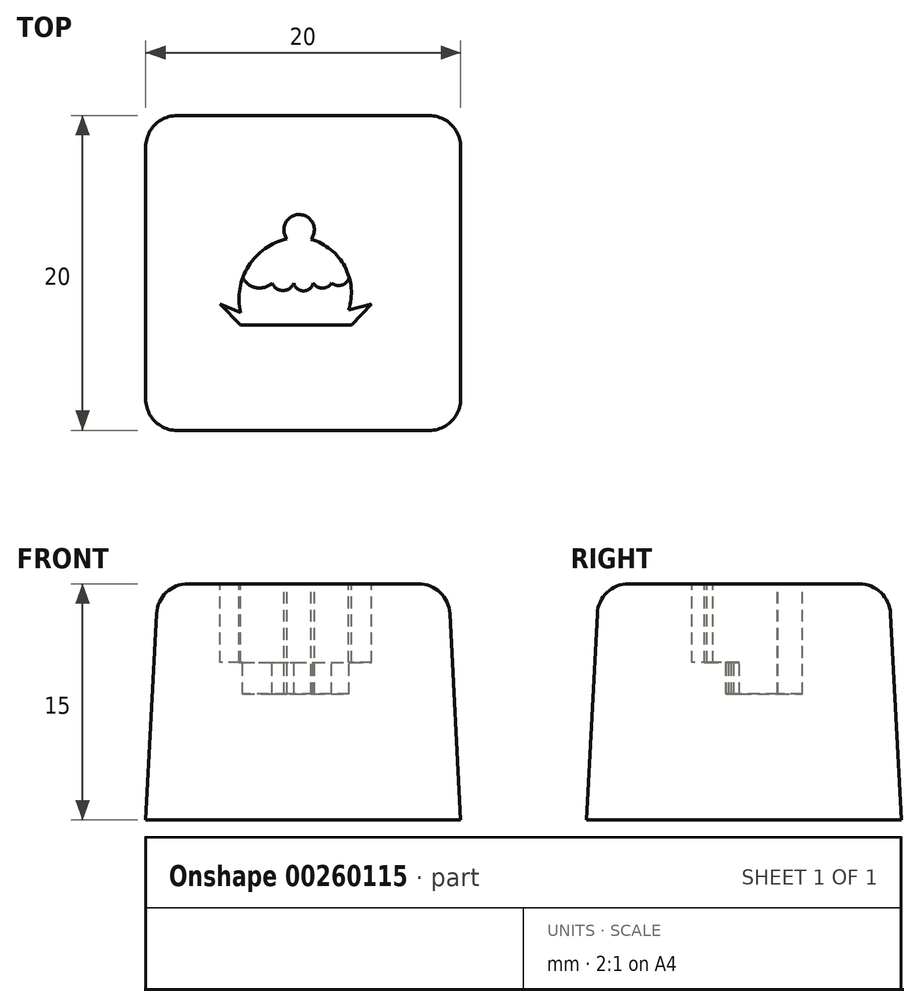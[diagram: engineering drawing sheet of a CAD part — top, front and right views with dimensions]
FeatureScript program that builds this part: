
annotation { "Feature Type Name" : "Feature", "Feature Type Description" : "" }
export const myFeature = defineFeature(function(context is Context, id is Id, definition is map)
    precondition{}
    {
        {
            var Q0;
            Q0=qCreatedBy(makeId("Top.planeOp"),FACE);
            var sketch = newSketch(context, id + "F0", { "sketchPlane" : qUnion([Q0])});
            skLineSegment(sketch, "E0.bottom", {"start": v(-8.03, 10.29) * mm, "end": v(11.97, 10.29) * mm});
            skLineSegment(sketch, "E0.top", {"start": v(-8.03, -9.71) * mm, "end": v(11.97, -9.71) * mm});
            skLineSegment(sketch, "E0.left", {"start": v(-8.03, 10.29) * mm, "end": v(-8.03, -9.71) * mm});
            skLineSegment(sketch, "E0.right", {"start": v(11.97, 10.29) * mm, "end": v(11.97, -9.71) * mm});
            skSolve(sketch);
        }
        {
            var Q0;
            Q0 = qSketchRegion(id + "F0", true);
            extrude(context, id + "F1", {"entities" : qUnion([Q0]), "depth" : 15 * mm, "hasDraft" : true, "draftAngle" : 3 * degree, "draftPullDirection" : true});
        }
        {
            var Q0;
            Q0=makeQuery(id+"F1.opExtrude","SWEPT_EDGE",EDGE,{"disambiguationData":[OSD([sQuery(id+"F0.wireOp",EDGE,"E0.bottom"),sQuery(id+"F0.wireOp",EDGE,"E0.right")])]});
            var Q1;
            Q1=makeQuery(id+"F1.opExtrude","CAP_EDGE",EDGE,{"disambiguationData":[OSD([sQuery(id+"F0.wireOp",EDGE,"E0.bottom")])],"isStart":false});
            var Q2;
            Q2=makeQuery(id+"F1.opExtrude","SWEPT_EDGE",EDGE,{"disambiguationData":[OSD([sQuery(id+"F0.wireOp",EDGE,"E0.bottom"),sQuery(id+"F0.wireOp",EDGE,"E0.left")])]});
            var Q3;
            Q3=makeQuery(id+"F1.opExtrude","CAP_EDGE",EDGE,{"disambiguationData":[OSD([sQuery(id+"F0.wireOp",EDGE,"E0.right")])],"isStart":false});
            var Q4;
            Q4=makeQuery(id+"F1.opExtrude","SWEPT_EDGE",EDGE,{"disambiguationData":[OSD([sQuery(id+"F0.wireOp",EDGE,"E0.top"),sQuery(id+"F0.wireOp",EDGE,"E0.right")])]});
            var Q5;
            Q5=makeQuery(id+"F1.opExtrude","CAP_EDGE",EDGE,{"disambiguationData":[OSD([sQuery(id+"F0.wireOp",EDGE,"E0.top")])],"isStart":false});
            var Q6;
            Q6=makeQuery(id+"F1.opExtrude","CAP_EDGE",EDGE,{"disambiguationData":[OSD([sQuery(id+"F0.wireOp",EDGE,"E0.left")])],"isStart":false});
            var Q7;
            Q7=makeQuery(id+"F1.opExtrude","SWEPT_EDGE",EDGE,{"disambiguationData":[OSD([sQuery(id+"F0.wireOp",EDGE,"E0.top"),sQuery(id+"F0.wireOp",EDGE,"E0.left")])]});
            fillet(context, id + "F2", {"entities" : qUnion([Q0, Q1, Q2, Q3, Q4, Q5, Q6, Q7]), "radius" : 2 * mm, "tangentPropagation" : true, "allowEdgeOverflow" : false});
        }
        {
            var Q0;
            Q0=makeQuery(id+"F1.opExtrude","CAP_FACE",FACE,{"disambiguationData":[OSD([sQuery(id+"F0.wireOp",EDGE,"E0.bottom"),sQuery(id+"F0.wireOp",EDGE,"E0.top"),sQuery(id+"F0.wireOp",EDGE,"E0.left"),sQuery(id+"F0.wireOp",EDGE,"E0.right")])],"isStart":false});
            var sketch = newSketch(context, id + "F3", { "sketchPlane" : qUnion([Q0])});
            skCircle(sketch, "E1", {"center": v(1.71, 3.03) * mm, "radius": 0.97 * mm});
            skArc(sketch, "E2", {"start": v(0.94, 2.45) * mm, "mid": v(-1.5, 0.73) * mm, "end": v(-2, -2.22) * mm});
            skArc(sketch, "E3", {"start": v(4.86, -2.07) * mm, "mid": v(4.62, 0.68) * mm, "end": v(2.47, 2.42) * mm});
            skLineSegment(sketch, "E4", {"start": v(-2, -2.22) * mm, "end": v(-3.3, -1.67) * mm});
            skLineSegment(sketch, "E5", {"start": v(-3.3, -1.67) * mm, "end": v(-2, -3.01) * mm});
            skLineSegment(sketch, "E6", {"start": v(-2, -3.01) * mm, "end": v(5.03, -3.01) * mm});
            skLineSegment(sketch, "E7", {"start": v(5.03, -3.01) * mm, "end": v(6.33, -1.67) * mm});
            skLineSegment(sketch, "E8", {"start": v(6.33, -1.67) * mm, "end": v(4.86, -2.07) * mm});
            skSolve(sketch);
        }
        {
            var Q0;
            Q0 = qSketchRegion(id + "F3", true);
            extrude(context, id + "F4", {"entities" : qUnion([Q0]), "operationType" : NewBodyOperationType.REMOVE, "oppositeDirection" : true, "depth" : 5 * mm});
        }
        {
            var Q0;
            Q0=makeQuery(id+"F4.boolean.opBoolean","COPY",FACE,{"derivedFrom":makeQuery(id+"F4.opExtrude","CAP_FACE",FACE,{"disambiguationData":[OSD([sQuery(id+"F3.wireOp",EDGE,"E1"),sQuery(id+"F3.wireOp",EDGE,"E2"),sQuery(id+"F3.wireOp",EDGE,"E3"),sQuery(id+"F3.wireOp",EDGE,"E4"),sQuery(id+"F3.wireOp",EDGE,"E5"),sQuery(id+"F3.wireOp",EDGE,"E6"),sQuery(id+"F3.wireOp",EDGE,"E7"),sQuery(id+"F3.wireOp",EDGE,"E8")])],"isStart":false})});
            var sketch = newSketch(context, id + "F5", { "sketchPlane" : qUnion([Q0])});
            skArc(sketch, "E9", {"start": v(-1.87, 0) * mm, "mid": v(-1.02, -0.65) * mm, "end": v(0, -0.35) * mm});
            skArc(sketch, "E10", {"start": v(0, -0.35) * mm, "mid": v(0.69, -0.83) * mm, "end": v(1.38, -0.35) * mm});
            skArc(sketch, "E11", {"start": v(1.38, -0.35) * mm, "mid": v(2, -0.85) * mm, "end": v(2.61, -0.35) * mm});
            skArc(sketch, "E12", {"start": v(2.61, -0.35) * mm, "mid": v(3.2, -0.68) * mm, "end": v(3.78, -0.35) * mm});
            skArc(sketch, "E13", {"start": v(3.78, -0.35) * mm, "mid": v(4.43, -0.48) * mm, "end": v(4.9, 0) * mm});
            skSolve(sketch);
        }
        {
            var Q0;
            {var subQ1=sQuery(id+"F5.wireOp",EDGE,"E9");Q0=makeQuery(id+"F5.imprint","IMPRINT",FACE,{"disambiguationData":[TD([[makeQuery(id+"F5.imprint","IMPRINT",EDGE,{"derivedFrom":subQ1}),1.0]])]});}
            extrude(context, id + "F6", {"entities" : qUnion([Q0]), "operationType" : NewBodyOperationType.REMOVE, "oppositeDirection" : true, "depth" : 2 * mm});
        }
    });
